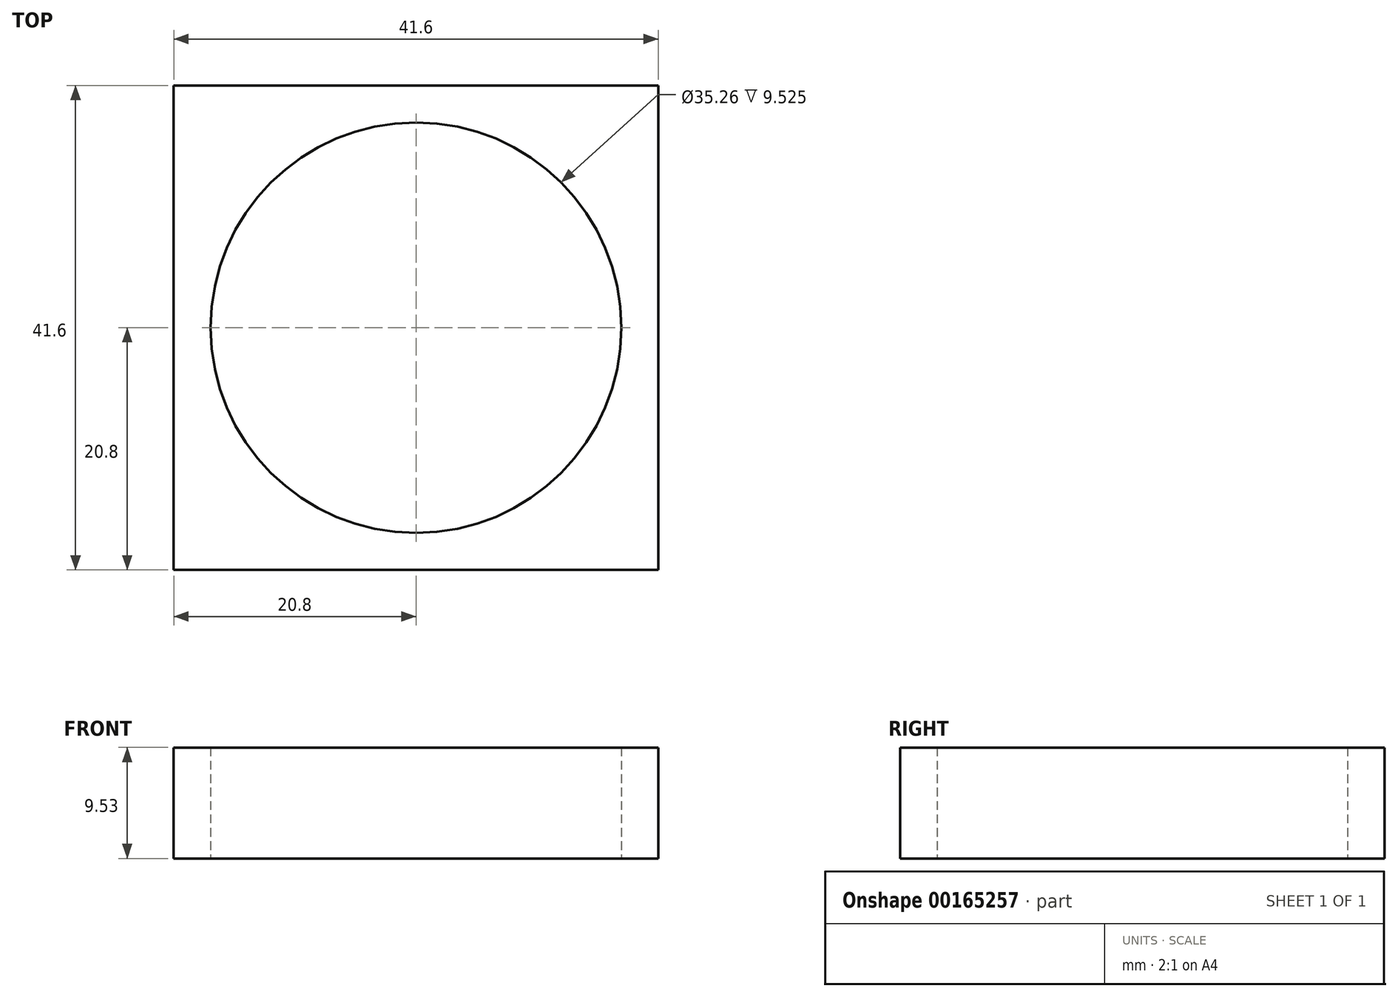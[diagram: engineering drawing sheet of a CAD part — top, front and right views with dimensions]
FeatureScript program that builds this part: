
annotation { "Feature Type Name" : "Feature", "Feature Type Description" : "" }
export const myFeature = defineFeature(function(context is Context, id is Id, definition is map)
    precondition{}
    {
        {
            var Q0;
            Q0=qCreatedBy(makeId("Top.planeOp"),FACE);
            var sketch = newSketch(context, id + "F0", { "sketchPlane" : qUnion([Q0])});
            skLineSegment(sketch, "E0.bottom", {"start": v(20.8, -20.8) * mm, "end": v(-20.8, -20.8) * mm});
            skLineSegment(sketch, "E0.top", {"start": v(20.8, 20.8) * mm, "end": v(-20.8, 20.8) * mm});
            skLineSegment(sketch, "E0.left", {"start": v(20.8, -20.8) * mm, "end": v(20.8, 20.8) * mm});
            skLineSegment(sketch, "E0.right", {"start": v(-20.8, -20.8) * mm, "end": v(-20.8, 20.8) * mm});
            skPoint(sketch, "E0.middle", {"position": v(0, 0) * mm});
            skCircle(sketch, "E1", {"center": v(0, 0) * mm, "radius": 17.63 * mm});
            skSolve(sketch);
        }
        {
            var Q0;
            Q0 = qSketchRegion(id + "F0", true);
            extrude(context, id + "F1", {"entities" : qUnion([Q0]), "depth" : 9.52 * mm});
        }
    });
